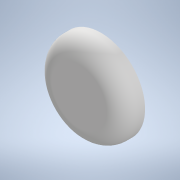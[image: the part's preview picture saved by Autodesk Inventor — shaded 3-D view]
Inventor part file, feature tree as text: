
AUTODESK INVENTOR PART (.ipt)
format: ipt  version: 2020.2 (Build 242310000, 310)  size: 120,832 bytes
history: native  units: in
note: dims shown in document units (in); Inventor stores cm internally (conversion verified against a paired STEP export)
features: revolve x1, fillet x1, sketch x1
ambient origin geometry x8: Origin, YZ Plane, XZ Plane, XY Plane, X Axis, Y Axis, Z Axis, Center Point
bodies: Solid1 (feature_tree)
feature tree (3):
  revolve  "Revolution1"  [1 undecoded]
  fillet  "Fillet1"  [1 undecoded]
  sketch  "Sketch1"  dims[d0=1.5748in d1=0.7874in d2=90.0deg d3=0.5906in]
note: 2 required parameter values undecoded (feature->parameter linkage not recoverable at this tier; creation-order binding heuristic only, values carry confidence <= 0.55)